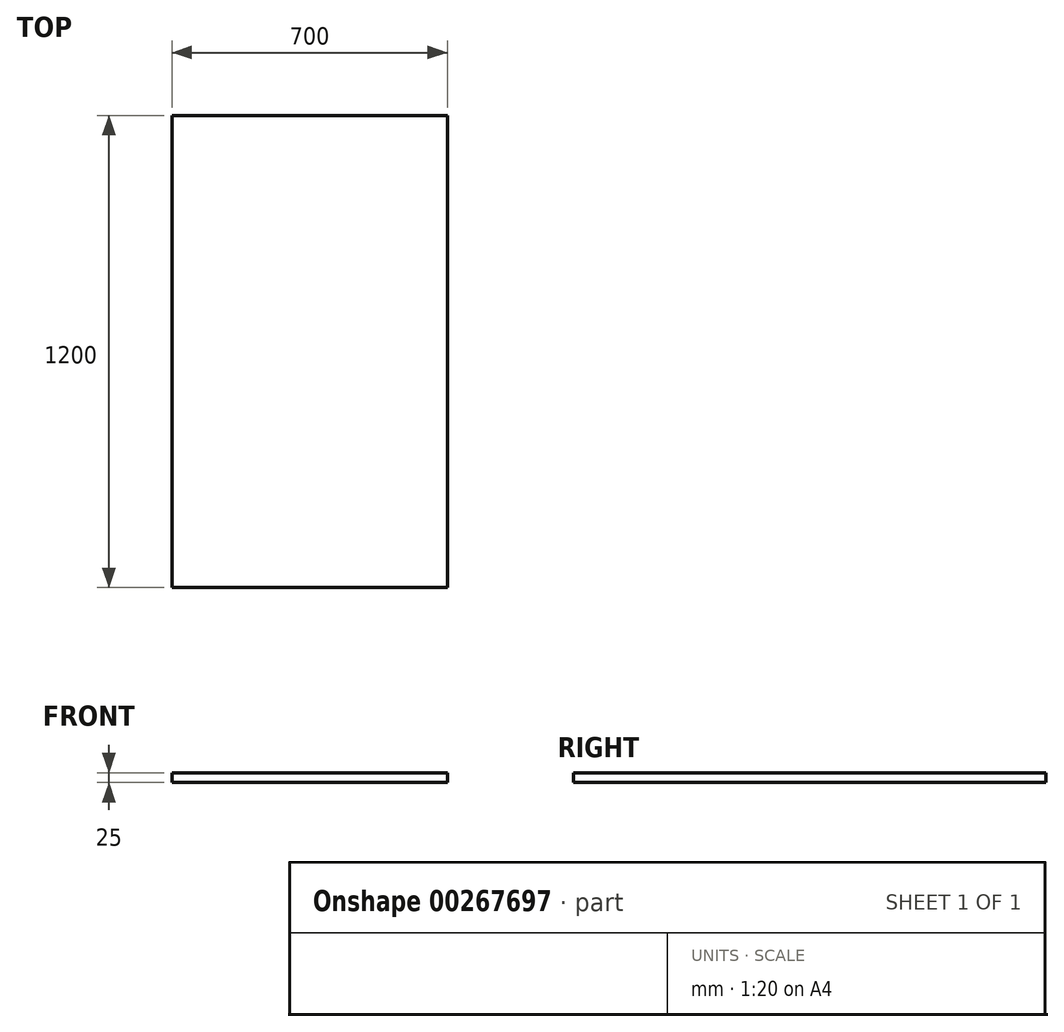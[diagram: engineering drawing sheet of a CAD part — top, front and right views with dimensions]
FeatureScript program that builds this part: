
annotation { "Feature Type Name" : "Feature", "Feature Type Description" : "" }
export const myFeature = defineFeature(function(context is Context, id is Id, definition is map)
    precondition{}
    {
        {
            var Q0;
            Q0=qCreatedBy(makeId("Top.planeOp"),FACE);
            var sketch = newSketch(context, id + "F0", { "sketchPlane" : qUnion([Q0])});
            skLineSegment(sketch, "E0.bottom", {"start": v(350, 600) * mm, "end": v(-350, 600) * mm});
            skLineSegment(sketch, "E0.top", {"start": v(350, -600) * mm, "end": v(-350, -600) * mm});
            skLineSegment(sketch, "E0.left", {"start": v(350, 600) * mm, "end": v(350, -600) * mm});
            skLineSegment(sketch, "E0.right", {"start": v(-350, 600) * mm, "end": v(-350, -600) * mm});
            skPoint(sketch, "E0.middle", {"position": v(0, 0) * mm});
            skSolve(sketch);
        }
        {
            var Q0;
            Q0=makeQuery(id+"F0.imprint","IMPRINT",FACE,{"disambiguationData":[TD([[makeQuery(id+"F0.imprint","IMPRINT",EDGE,{"derivedFrom":sQuery(id+"F0.wireOp",EDGE,"E0.bottom")}),1.0]])]});
            extrude(context, id + "F1", {"entities" : qUnion([Q0]), "oppositeDirection" : true, "depth" : 25 * mm});
        }
    });
